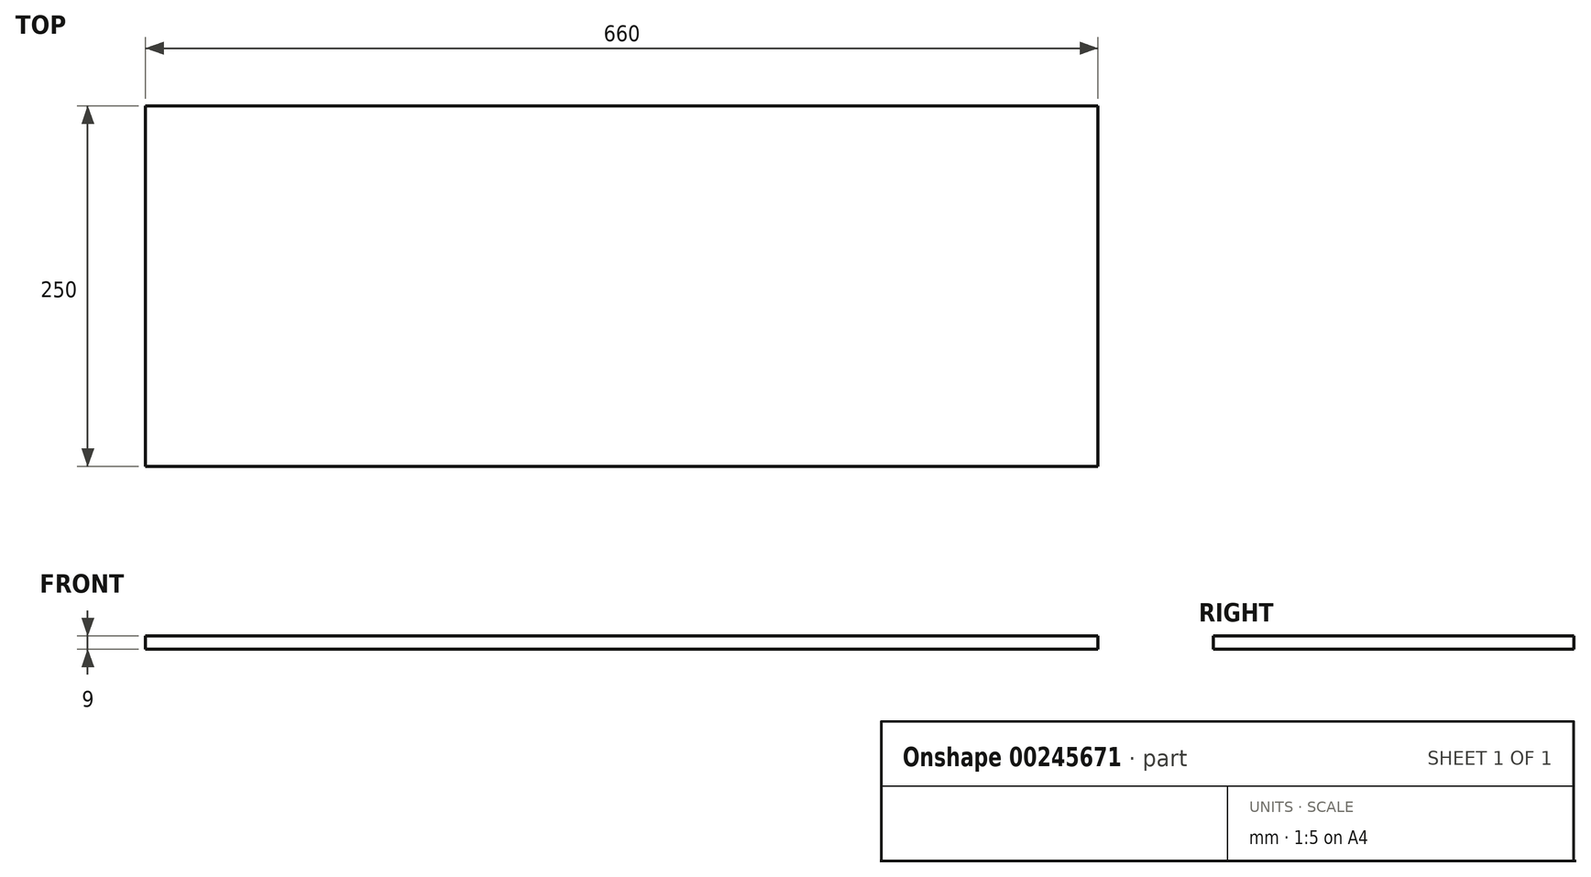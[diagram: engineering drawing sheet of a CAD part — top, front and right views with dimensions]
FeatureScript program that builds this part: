
annotation { "Feature Type Name" : "Feature", "Feature Type Description" : "" }
export const myFeature = defineFeature(function(context is Context, id is Id, definition is map)
    precondition{}
    {
        {
            var Q0;
            Q0=qCreatedBy(makeId("Top.planeOp"),FACE);
            var sketch = newSketch(context, id + "F0", { "sketchPlane" : qUnion([Q0])});
            skLineSegment(sketch, "E0.bottom", {"start": v(330, 125) * mm, "end": v(-330, 125) * mm});
            skLineSegment(sketch, "E0.top", {"start": v(330, -125) * mm, "end": v(-330, -125) * mm});
            skLineSegment(sketch, "E0.left", {"start": v(330, 125) * mm, "end": v(330, -125) * mm});
            skLineSegment(sketch, "E0.right", {"start": v(-330, 125) * mm, "end": v(-330, -125) * mm});
            skPoint(sketch, "E0.middle", {"position": v(0, 0) * mm});
            skSolve(sketch);
        }
        {
            var Q0;
            Q0 = qSketchRegion(id + "F0", true);
            extrude(context, id + "F1", {"entities" : qUnion([Q0]), "depth" : 9 * mm});
        }
    });
